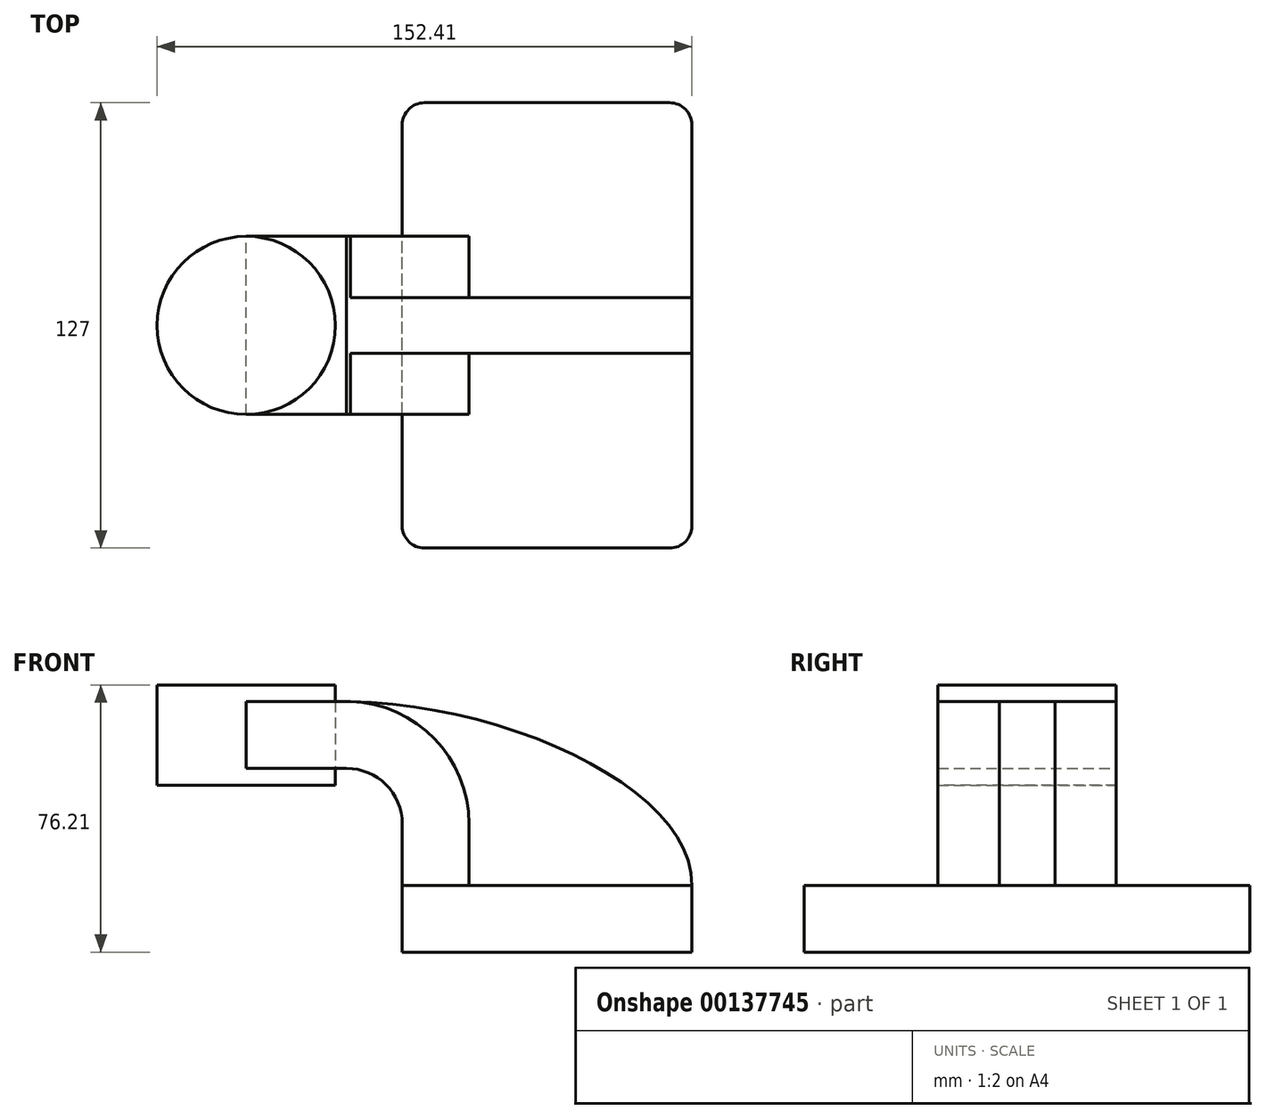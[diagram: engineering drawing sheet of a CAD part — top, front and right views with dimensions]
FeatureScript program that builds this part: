
annotation { "Feature Type Name" : "Feature", "Feature Type Description" : "" }
export const myFeature = defineFeature(function(context is Context, id is Id, definition is map)
    precondition{}
    {
        {
            var Q0;
            Q0=qCreatedBy(makeId("Front.planeOp"),FACE);
            var sketch = newSketch(context, id + "F0", { "sketchPlane" : qUnion([Q0])});
            skLineSegment(sketch, "E0.bottom", {"start": v(-41.28, -9.53) * mm, "end": v(41.28, -9.53) * mm});
            skLineSegment(sketch, "E0.top", {"start": v(-41.28, 9.52) * mm, "end": v(41.28, 9.52) * mm});
            skLineSegment(sketch, "E0.left", {"start": v(-41.28, -9.53) * mm, "end": v(-41.28, 9.52) * mm});
            skLineSegment(sketch, "E0.right", {"start": v(41.28, -9.53) * mm, "end": v(41.28, 9.52) * mm});
            skPoint(sketch, "E0.middle", {"position": v(0, 0) * mm});
            skLineSegment(sketch, "E1.bottom", {"start": v(-111.13, 66.67) * mm, "end": v(-60.33, 66.67) * mm});
            skLineSegment(sketch, "E1.top", {"start": v(-111.13, 38.1) * mm, "end": v(-60.33, 38.1) * mm});
            skLineSegment(sketch, "E1.left", {"start": v(-111.13, 66.67) * mm, "end": v(-111.13, 38.1) * mm});
            skLineSegment(sketch, "E1.right", {"start": v(-60.33, 66.67) * mm, "end": v(-60.33, 38.1) * mm});
            skPoint(sketch, "E1.middle", {"position": v(-85.73, 52.39) * mm});
            skLineSegment(sketch, "E2", {"start": v(-41.28, 9.52) * mm, "end": v(-41.28, 27) * mm});
            skArc(sketch, "E3", {"start": v(-41.28, 27) * mm, "mid": v(-45.92, 38.23) * mm, "end": v(-57.15, 42.88) * mm});
            skLineSegment(sketch, "E4", {"start": v(-57.15, 42.88) * mm, "end": v(-85.73, 42.88) * mm});
            skLineSegment(sketch, "E5.0", {"start": v(-57.15, 61.93) * mm, "end": v(-85.73, 61.93) * mm});
            skArc(sketch, "E5.1", {"start": v(-22.23, 27) * mm, "mid": v(-32.45, 51.7) * mm, "end": v(-57.15, 61.93) * mm});
            skLineSegment(sketch, "E5.2", {"start": v(-22.23, 9.52) * mm, "end": v(-22.23, 27) * mm});
            skFitSpline(sketch, "E6", {"points": [v(41.28, 9.52) * mm, v(-57.15, 61.93) * mm], "startDerivative": vector(1.17, 82.26) * mm, "endDerivative": vector(-138.12, 1.61) * mm});
            skLineSegment(sketch, "E7", {"start": v(-85.73, 38.1) * mm, "end": v(-85.73, 66.67) * mm});
            skSolve(sketch);
        }
        {
            var Q0;
            Q0=makeQuery(id+"F0.imprint","IMPRINT",FACE,{"disambiguationData":[TD([[makeQuery(id+"F0.imprint","IMPRINT",EDGE,{"derivedFrom":sQuery(id+"F0.wireOp",EDGE,"E0.bottom")}),1.0]])]});
            extrude(context, id + "F1", {"entities" : qUnion([Q0]), "endBound" : BoundingType.SYMMETRIC, "depth" : 127 * mm});
        }
        {
            var Q0;
            {var subQ6=sQuery(id+"F0.wireOp",EDGE,"E2");Q0=makeQuery(id+"F0.imprint","IMPRINT",FACE,{"disambiguationData":[TD([[makeQuery(id+"F0.imprint","IMPRINT",EDGE,{"derivedFrom":subQ6}),-1.0]])]});}
            var Q1;
            {var subQ0=sQuery(id+"F0.wireOp",EDGE,"E5.0");var subQ1=sQuery(id+"F0.wireOp",EDGE,"E1.right");var subQ2=makeQuery(id+"F0.imprint","INTERSECT",VERTEX,{"derivedFrom":[subQ1,subQ0]});Q1=makeQuery(id+"F0.imprint","IMPRINT",FACE,{"disambiguationData":[TD([[makeQuery(id+"F0.imprint","IMPRINT",EDGE,{"disambiguationData":[TD([[subQ2,-1.0]])],"derivedFrom":subQ1}),-1.0]])]});}
            extrude(context, id + "F2", {"entities" : qUnion([Q0, Q1]), "operationType" : NewBodyOperationType.ADD, "endBound" : BoundingType.SYMMETRIC, "depth" : 50.8 * mm});
        }
        {
            var Q0;
            {var subQ3=sQuery(id+"F0.wireOp",EDGE,"E5.2");Q0=makeQuery(id+"F0.imprint","IMPRINT",FACE,{"disambiguationData":[TD([[makeQuery(id+"F0.imprint","IMPRINT",EDGE,{"derivedFrom":subQ3}),-1.0]])]});}
            extrude(context, id + "F3", {"entities" : qUnion([Q0]), "operationType" : NewBodyOperationType.ADD, "endBound" : BoundingType.SYMMETRIC, "depth" : 15.88 * mm});
        }
        {
            var Q0;
            {var subQ4=sQuery(id+"F0.wireOp",EDGE,"E1.left");Q0=makeQuery(id+"F0.imprint","IMPRINT",FACE,{"disambiguationData":[TD([[makeQuery(id+"F0.imprint","IMPRINT",EDGE,{"derivedFrom":subQ4}),1.0]])]});}
            var Q1;
            Q1=sQuery(id+"F0.wireOp",EDGE,"E7");
            revolve(context, id + "F4", {"entities" : qUnion([Q0]), "axis" : qUnion([Q1]), "revolveType" : RevolveType.FULL});
        }
        {
            var Q0;
            Q0=makeQuery(id+"F1.opExtrude","CAP_EDGE",EDGE,{"disambiguationData":[OSD([sQuery(id+"F0.wireOp",EDGE,"E0.left")])],"isStart":true});
            var Q1;
            Q1=makeQuery(id+"F1.opExtrude","CAP_EDGE",EDGE,{"disambiguationData":[OSD([sQuery(id+"F0.wireOp",EDGE,"E0.right")])],"isStart":true});
            var Q2;
            Q2=makeQuery(id+"F1.opExtrude","CAP_EDGE",EDGE,{"disambiguationData":[OSD([sQuery(id+"F0.wireOp",EDGE,"E0.left")])],"isStart":false});
            var Q3;
            Q3=makeQuery(id+"F1.opExtrude","CAP_EDGE",EDGE,{"disambiguationData":[OSD([sQuery(id+"F0.wireOp",EDGE,"E0.right")])],"isStart":false});
            fillet(context, id + "F5", {"entities" : qUnion([Q0, Q1, Q2, Q3]), "radius" : 6.35 * mm, "tangentPropagation" : true, "allowEdgeOverflow" : false});
        }
    });
